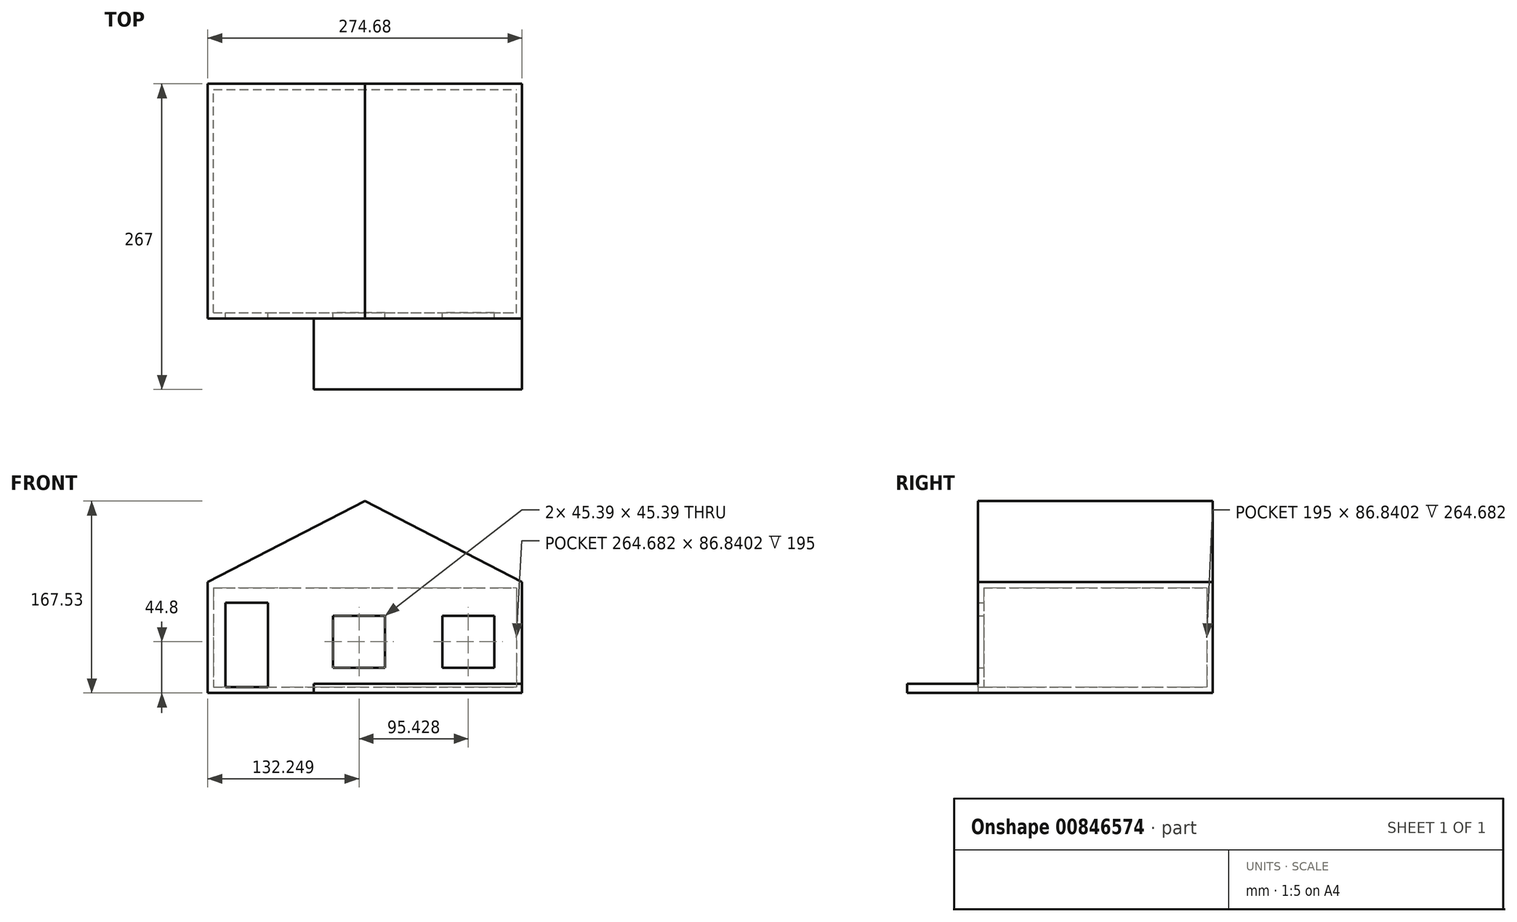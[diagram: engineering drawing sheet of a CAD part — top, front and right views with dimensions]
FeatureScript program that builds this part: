
annotation { "Feature Type Name" : "Feature", "Feature Type Description" : "" }
export const myFeature = defineFeature(function(context is Context, id is Id, definition is map)
    precondition{}
    {
        {
            var Q0;
            Q0=qCreatedBy(makeId("Front.planeOp"),FACE);
            var sketch = newSketch(context, id + "F0", { "sketchPlane" : qUnion([Q0])});
            skLineSegment(sketch, "E0.bottom", {"start": v(-137.34, 48.42) * mm, "end": v(137.34, 48.42) * mm});
            skLineSegment(sketch, "E0.top", {"start": v(-137.34, -48.42) * mm, "end": v(137.34, -48.42) * mm});
            skLineSegment(sketch, "E0.left", {"start": v(-137.34, 48.42) * mm, "end": v(-137.34, -48.42) * mm});
            skLineSegment(sketch, "E0.right", {"start": v(137.34, 48.42) * mm, "end": v(137.34, -48.42) * mm});
            skPoint(sketch, "E0.middle", {"position": v(0, 0) * mm});
            skSolve(sketch);
        }
        {
            var Q0;
            Q0 = qSketchRegion(id + "F0", true);
            extrude(context, id + "F1", {"entities" : qUnion([Q0]), "depth" : 200 * mm, "offsetDistance" : 25 * mm});
        }
        {
            var Q0;
            Q0=makeQuery(id+"F1.opExtrude","CAP_FACE",FACE,{"disambiguationData":[OSD([sQuery(id+"F0.wireOp",EDGE,"E0.bottom"),sQuery(id+"F0.wireOp",EDGE,"E0.top"),sQuery(id+"F0.wireOp",EDGE,"E0.left"),sQuery(id+"F0.wireOp",EDGE,"E0.right")])],"isStart":false});
            shell(context, id + "F2", {"entities" : qUnion([Q0]), "thickness" : 5 * mm});
        }
        {
            var Q0;
            Q0=makeQuery(id+"F1.opExtrude","CAP_FACE",FACE,{"disambiguationData":[OSD([sQuery(id+"F0.wireOp",EDGE,"E0.bottom"),sQuery(id+"F0.wireOp",EDGE,"E0.top"),sQuery(id+"F0.wireOp",EDGE,"E0.left"),sQuery(id+"F0.wireOp",EDGE,"E0.right")])],"isStart":false});
            var sketch = newSketch(context, id + "F3", { "sketchPlane" : qUnion([Q0])});
            skLineSegment(sketch, "E1", {"start": v(-137.34, 48.42) * mm, "end": v(137.34, 48.42) * mm});
            skLineSegment(sketch, "E2", {"start": v(137.34, 48.42) * mm, "end": v(137.34, -48.42) * mm});
            skLineSegment(sketch, "E3", {"start": v(137.34, -48.42) * mm, "end": v(-137.34, -48.42) * mm});
            skLineSegment(sketch, "E4", {"start": v(-137.34, -48.42) * mm, "end": v(-137.34, 48.42) * mm});
            skLineSegment(sketch, "E5", {"start": v(-121.7, -43.42) * mm, "end": v(-121.7, 30.42) * mm});
            skLineSegment(sketch, "E6", {"start": v(-121.7, 30.42) * mm, "end": v(-84.57, 30.42) * mm});
            skLineSegment(sketch, "E7", {"start": v(-84.57, 30.42) * mm, "end": v(-84.57, -43.42) * mm});
            skLineSegment(sketch, "E8", {"start": v(-84.57, -43.42) * mm, "end": v(-121.7, -43.42) * mm});
            skLineSegment(sketch, "E9", {"start": v(-27.79, 19.08) * mm, "end": v(-27.79, -26.32) * mm});
            skLineSegment(sketch, "E10", {"start": v(-27.79, -26.32) * mm, "end": v(17.6, -26.32) * mm});
            skLineSegment(sketch, "E11", {"start": v(17.6, -26.32) * mm, "end": v(17.6, 19.08) * mm});
            skLineSegment(sketch, "E12", {"start": v(17.6, 19.08) * mm, "end": v(-27.79, 19.08) * mm});
            skLineSegment(sketch, "E13", {"start": v(67.64, 19.08) * mm, "end": v(67.64, -26.32) * mm});
            skLineSegment(sketch, "E14", {"start": v(67.64, -26.32) * mm, "end": v(113.03, -26.32) * mm});
            skLineSegment(sketch, "E15", {"start": v(113.03, -26.32) * mm, "end": v(113.03, 19.08) * mm});
            skLineSegment(sketch, "E16", {"start": v(113.03, 19.08) * mm, "end": v(67.64, 19.08) * mm});
            skSolve(sketch);
        }
        {
            var Q0;
            Q0 = qSketchRegion(id + "F3", true);
            extrude(context, id + "F4", {"entities" : qUnion([Q0]), "operationType" : NewBodyOperationType.ADD, "depth" : 5 * mm, "offsetDistance" : 25 * mm});
        }
        {
            var Q0;
            Q0=makeQuery(id+"F1.opExtrude","CAP_FACE",FACE,{"disambiguationData":[OSD([sQuery(id+"F0.wireOp",EDGE,"E0.bottom"),sQuery(id+"F0.wireOp",EDGE,"E0.top"),sQuery(id+"F0.wireOp",EDGE,"E0.left"),sQuery(id+"F0.wireOp",EDGE,"E0.right")])],"isStart":true});
            var sketch = newSketch(context, id + "F5", { "sketchPlane" : qUnion([Q0])});
            skLineSegment(sketch, "E17", {"start": v(-137.34, 48.42) * mm, "end": v(0, 119.11) * mm});
            skLineSegment(sketch, "E18", {"start": v(0, 119.11) * mm, "end": v(137.34, 48.42) * mm});
            skLineSegment(sketch, "E19", {"start": v(137.34, 48.42) * mm, "end": v(-137.34, 48.42) * mm});
            skSolve(sketch);
        }
        {
            var Q0;
            Q0=makeQuery(id+"F5.imprint","IMPRINT",FACE,{"disambiguationData":[TD([[makeQuery(id+"F5.imprint","IMPRINT",EDGE,{"derivedFrom":sQuery(id+"F5.wireOp",EDGE,"E17")}),-1.0]])]});
            extrude(context, id + "F6", {"entities" : qUnion([Q0]), "operationType" : NewBodyOperationType.ADD, "oppositeDirection" : true, "depth" : 205 * mm, "offsetDistance" : 25 * mm});
        }
        {
            var Q0;
            Q0=makeQuery(id+"F4.boolean.opBoolean","MERGE",FACE,{"derivedFrom":[makeQuery(id+"F1.opExtrude","SWEPT_FACE",FACE,{"disambiguationData":[OSD([sQuery(id+"F0.wireOp",EDGE,"E0.top")])]}),makeQuery(id+"F4.opExtrude","SWEPT_FACE",FACE,{"disambiguationData":[OSD([sQuery(id+"F3.wireOp",EDGE,"E3")])]})]});
            var sketch = newSketch(context, id + "F7", { "sketchPlane" : qUnion([Q0])});
            skLineSegment(sketch, "E20", {"start": v(137.34, 205) * mm, "end": v(137.34, 267) * mm});
            skLineSegment(sketch, "E21", {"start": v(137.34, 267) * mm, "end": v(-44.66, 267) * mm});
            skLineSegment(sketch, "E22", {"start": v(-44.66, 267) * mm, "end": v(-44.66, 205) * mm});
            skLineSegment(sketch, "E23", {"start": v(-44.66, 205) * mm, "end": v(137.34, 205) * mm});
            skSolve(sketch);
        }
        {
            var Q0;
            Q0 = qSketchRegion(id + "F7", true);
            extrude(context, id + "F8", {"entities" : qUnion([Q0]), "operationType" : NewBodyOperationType.ADD, "oppositeDirection" : true, "depth" : 8 * mm, "offsetDistance" : 25 * mm});
        }
    });
